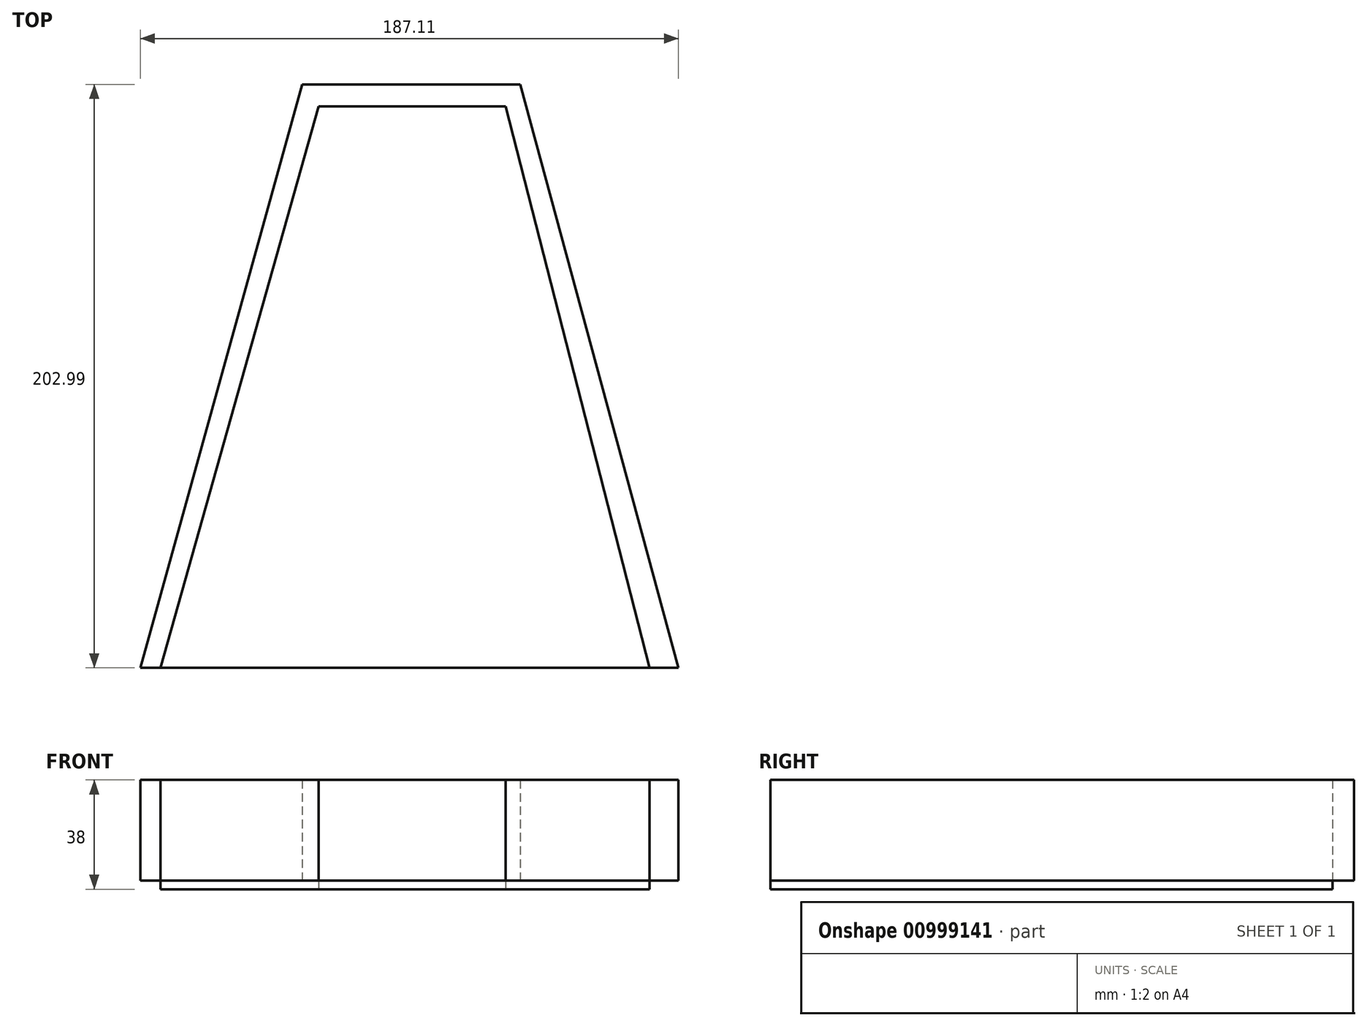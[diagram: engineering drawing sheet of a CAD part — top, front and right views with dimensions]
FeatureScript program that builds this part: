
annotation { "Feature Type Name" : "Feature", "Feature Type Description" : "" }
export const myFeature = defineFeature(function(context is Context, id is Id, definition is map)
    precondition{}
    {
        {
            var Q0;
            Q0=qCreatedBy(makeId("Top.planeOp"),FACE);
            var sketch = newSketch(context, id + "F0", { "sketchPlane" : qUnion([Q0])});
            skLineSegment(sketch, "E0", {"start": v(-35, 195.41) * mm, "end": v(-90, 0) * mm});
            skLineSegment(sketch, "E1", {"start": v(-35, 195.41) * mm, "end": v(30, 195.41) * mm});
            skLineSegment(sketch, "E2", {"start": v(30, 195.41) * mm, "end": v(80, 0) * mm});
            skLineSegment(sketch, "E3", {"start": v(0, 0) * mm, "end": v(-90, 0) * mm});
            skLineSegment(sketch, "E4", {"start": v(0, 0) * mm, "end": v(80, 0) * mm});
            skSolve(sketch);
        }
        {
            var Q0;
            Q0=makeQuery(id+"F0.imprint","IMPRINT",FACE,{"disambiguationData":[TD([[makeQuery(id+"F0.imprint","IMPRINT",EDGE,{"derivedFrom":sQuery(id+"F0.wireOp",EDGE,"E0")}),1.0]])]});
            extrude(context, id + "F1", {"entities" : qUnion([Q0]), "depth" : 3 * mm, "offsetDistance" : 25 * mm});
        }
        {
            var Q0;
            Q0=qCreatedBy(makeId("Top.planeOp"),FACE);
            var sketch = newSketch(context, id + "F2", { "sketchPlane" : qUnion([Q0])});
            skLineSegment(sketch, "E5", {"start": v(0, 0) * mm, "end": v(0, 120.23) * mm});
            skCircle(sketch, "E6", {"center": v(0, 120.23) * mm, "radius": 10.44 * mm});
            skSolve(sketch);
        }
        {
            var Q0;
            Q0=makeQuery(id+"F2.imprint","IMPRINT",FACE,{"disambiguationData":[TD([[makeQuery(id+"F2.imprint","IMPRINT",EDGE,{"derivedFrom":sQuery(id+"F2.wireOp",EDGE,"E6")}),1.0]])]});
            extrude(context, id + "F3", {"entities" : qUnion([Q0]), "operationType" : NewBodyOperationType.REMOVE, "endBound" : BoundingType.THROUGH_ALL, "oppositeDirection" : true, "depth" : 25 * mm, "offsetDistance" : 25 * mm});
        }
        {
            var Q0;
            Q0=makeQuery(id+"F1.opExtrude","CAP_FACE",FACE,{"disambiguationData":[OSD([sQuery(id+"F0.wireOp",EDGE,"E0"),sQuery(id+"F0.wireOp",EDGE,"E1"),sQuery(id+"F0.wireOp",EDGE,"E2"),sQuery(id+"F0.wireOp",EDGE,"E3"),sQuery(id+"F0.wireOp",EDGE,"E4")])],"isStart":false});
            var sketch = newSketch(context, id + "F4", { "sketchPlane" : qUnion([Q0])});
            skLineSegment(sketch, "E7", {"start": v(-97.08, 0) * mm, "end": v(-40.82, 203) * mm});
            skLineSegment(sketch, "E8", {"start": v(-40.82, 203) * mm, "end": v(35.07, 203) * mm});
            skLineSegment(sketch, "E9", {"start": v(35.07, 203) * mm, "end": v(90.03, 0) * mm});
            skLineSegment(sketch, "E10", {"start": v(90.03, 0) * mm, "end": v(80, 0) * mm});
            skLineSegment(sketch, "E11", {"start": v(-97.08, 0) * mm, "end": v(-90, 0) * mm});
            skSolve(sketch);
        }
        {
            var Q0;
            Q0 = qSketchRegion(id + "F4", true);
            var Q1;
            Q1=makeQuery(id+"F4.imprint","IMPRINT",FACE,{"disambiguationData":[TD([[makeQuery(id+"F4.imprint","IMPRINT",EDGE,{"derivedFrom":sQuery(id+"F4.wireOp",EDGE,"E7")}),-1.0]])]});
            extrude(context, id + "F5", {"entities" : qUnion([Q0, Q1]), "depth" : 35 * mm, "offsetDistance" : 25 * mm});
        }
    });
